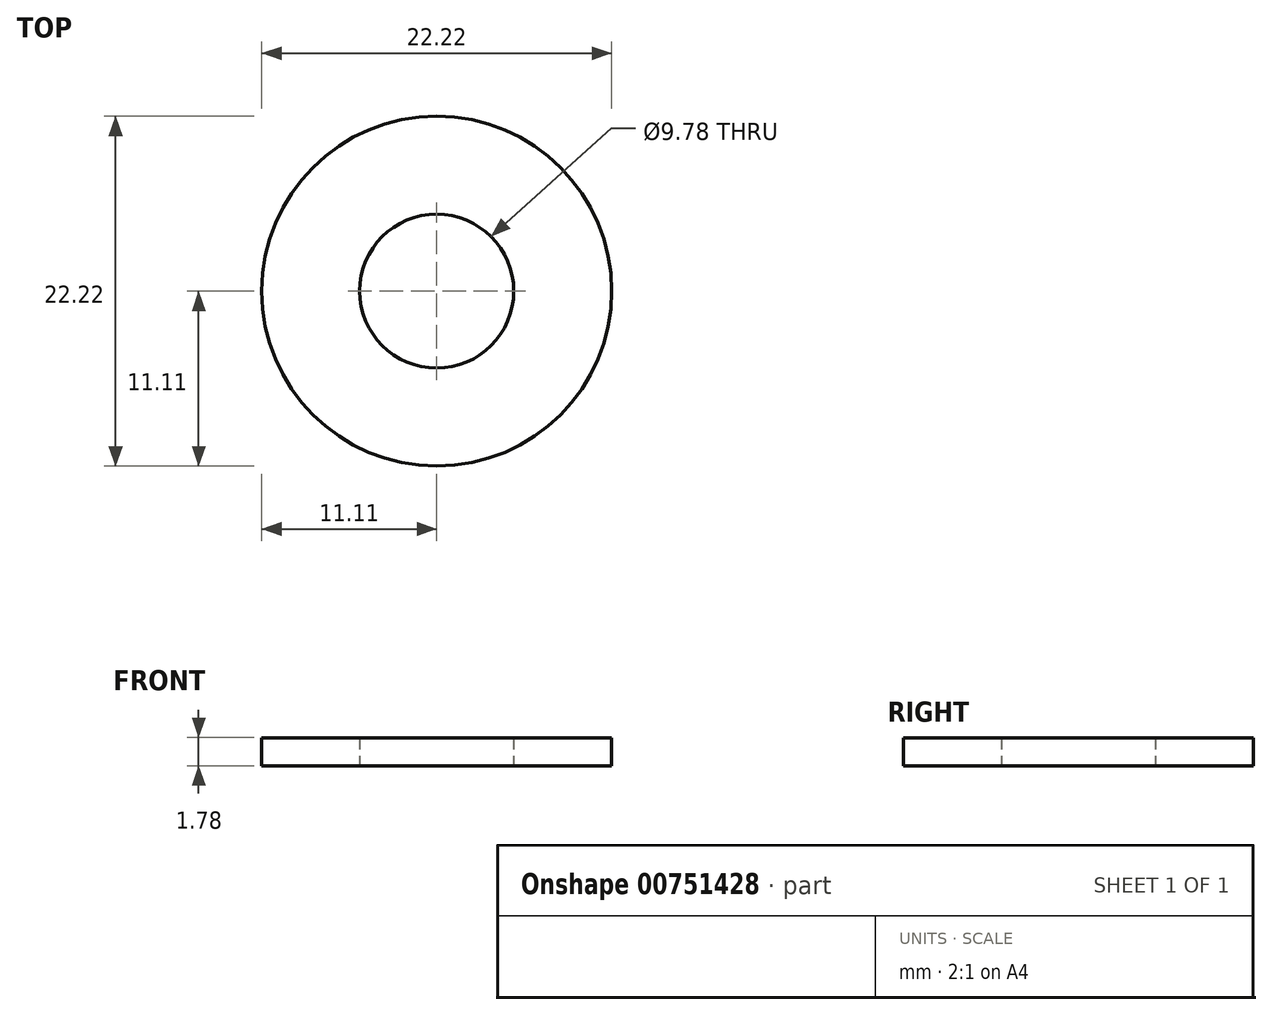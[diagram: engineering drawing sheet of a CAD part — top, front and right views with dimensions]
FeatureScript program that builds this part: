
annotation { "Feature Type Name" : "Feature", "Feature Type Description" : "" }
export const myFeature = defineFeature(function(context is Context, id is Id, definition is map)
    precondition{}
    {
        {
            var Q0;
            Q0=qCreatedBy(makeId("Top.planeOp"),FACE);
            var sketch = newSketch(context, id + "F0", { "sketchPlane" : qUnion([Q0])});
            skCircle(sketch, "E0", {"center": v(0, 0) * mm, "radius": 4.89 * mm});
            skCircle(sketch, "E1", {"center": v(0, 0) * mm, "radius": 11.11 * mm});
            skSolve(sketch);
        }
        {
            var Q0;
            Q0=makeQuery(id+"F0.imprint","IMPRINT",FACE,{"disambiguationData":[TD([[makeQuery(id+"F0.imprint","IMPRINT",EDGE,{"derivedFrom":sQuery(id+"F0.wireOp",EDGE,"E0")}),-1.0]])]});
            extrude(context, id + "F1", {"entities" : qUnion([Q0]), "depth" : 1.78 * mm, "offsetDistance" : 25.4 * mm});
        }
    });
